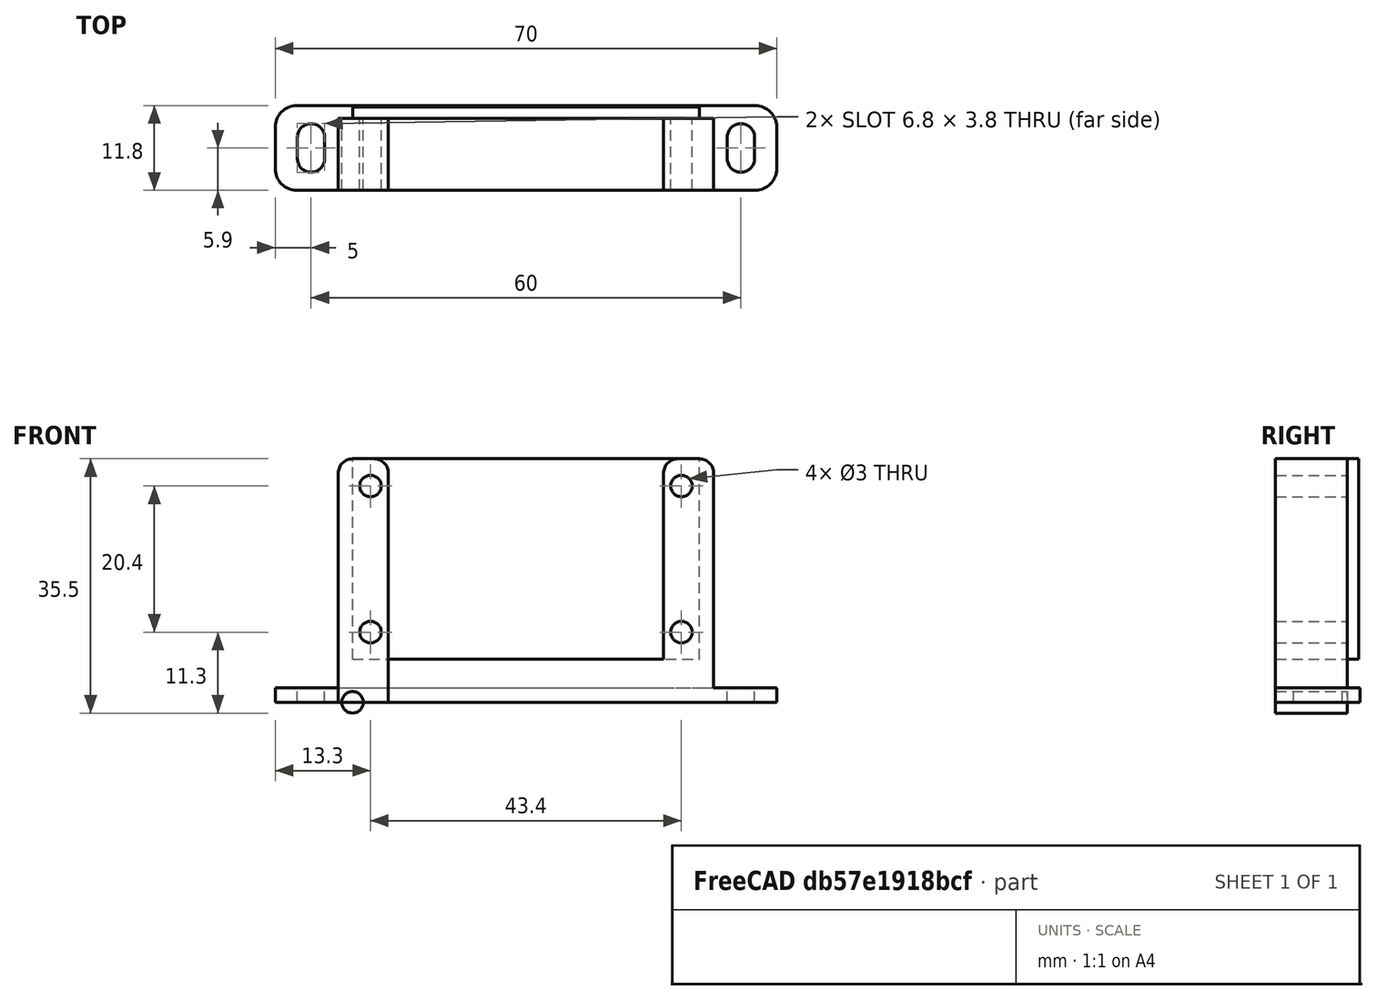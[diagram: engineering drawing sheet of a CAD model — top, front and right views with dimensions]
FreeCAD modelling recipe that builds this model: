
FCSTD DOCUMENT  (FreeCAD 0.19R)
Label: esp8266_wemos
License: All rights reserved
LicenseURL: http://en.wikipedia.org/wiki/All_rights_reserved
objects: Part::Box×3, Part::FeaturePython×2, Part::Cut×2, Spreadsheet::Sheet×1, Part::Cylinder×1, Part::Fillet×1, Part::Feature×1, Part::MultiFuse×1, PartDesign::FeatureBase×1, PartDesign::Body×1
note: 11 computed .brp shape members not serialized (recipe doc carries the construction recipe); baked Part::Feature solids carry a one-line shape summary decoded from their .brp

FEATURE [Part::Box] Box  label="v attachment"
  AttacherType = Attacher::AttachEngine3D
  Height = 34
  Length = 7
  Placement = pos=(-2,0,0) rot=(0,0,1;0rad)
  Width = 10
  expr: .Placement.Base.x = -(<<p>>.hole_stand_length - (<<p>>.pcb_length - <<p>>.hole_dist_length))
  expr: Length = <<p>>.hole_stand_length
  expr: Width = <<p>>.thickness
  expr: Height = <<p>>.pcb_width + <<p>>.bottom_offset
FEATURE [Spreadsheet::Sheet] Spreadsheet  label="p"
  cells = A1=pcb_length; B1(pcb_length)=48.4; A2=pcb_width; B2(pcb_width)=28; A3=pcb_height; B3(pcb_height)=1.6; A4=hole_dist_length; B4(hole_dist_length)=43.4; A5=hole_dist_width; B5(hole_dist_width)=20.4; A6=hole_r; B6(hole_r)=1.5; A7=thickness; B7(thickness)=10; A8=bottom_offset; B8(bottom_offset)=6; A9=hole_stand_length; B9(hole_stand_length)=7
FEATURE [Part::Box] Box001  label="bottom block"
  AttacherType = Attacher::AttachEngine3D
  Height = 6
  Length = 48.4
  Width = 10
  expr: Height = <<p>>.bottom_offset
  expr: Width = <<p>>.thickness
  expr: Length = <<p>>.pcb_length
FEATURE [Part::Box] Box002  label="pcb mockup body"
  AttacherType = Attacher::AttachEngine3D
  Height = 28
  Length = 48.4
  Placement = pos=(0,10,6) rot=(0,0,1;0rad)
  Width = 1.6
  expr: Length = <<p>>.pcb_length
  expr: Width = <<p>>.pcb_height
  expr: Height = <<p>>.pcb_width
  expr: .Placement.Base.z = <<p>>.bottom_offset
  expr: .Placement.Base.y = <<p>>.thickness
FEATURE [Part::Cylinder] Cylinder  label="hole"
  Angle = 360
  AttacherType = Attacher::AttachEngine3D
  Height = 10
  Placement = pos=(0,0,0) rot=(-1,0,0;1.5708rad)
  Radius = 1.5
  expr: Radius = <<p>>.hole_r
FEATURE [Part::FeaturePython] Array001  label="hole array"  # Draft array (typed FeaturePython)
  Angle = 360
  ArrayType = 0
  Axis = (0,0,1)
  Base = -> Cylinder
  Center = (0,0,0)
  Count = 4
  ExpandArray = false
  Fuse = false
  IntervalAxis = (0,0,0)
  IntervalX = (43.4,0,0)
  IntervalY = (0,100,0)
  IntervalZ = (0,0,20.4)
  NumberCircles = 3
  NumberPolar = 5
  NumberX = 2
  NumberY = 1
  NumberZ = 2
  Placement = pos=(2.5,0,9.8) rot=(0,0,1;0rad)
  PlacementList = 4 placements: [(0,0,0),(0,0,20.4),(43.4,0,0),(43.4,0,20.4)]
  RadialDistance = 50
  ScaleList = (4) [(1,1,1),(1,1,1),(1,1,1),(1,1,1)]
  Symmetry = 1
  TangentialDistance = 25
  expr: .IntervalX.x = <<p>>.hole_dist_length
  expr: .IntervalZ.z = <<p>>.hole_dist_width
  expr: .Placement.Base.z = <<p>>.bottom_offset + (<<p>>.pcb_width - <<p>>.hole_dist_width) / 2
  expr: .Placement.Base.x = (<<p>>.pcb_length - <<p>>.hole_dist_length) / 2
FEATURE [Part::Fillet] Fillet  label="v attachment fillet"
  Base = -> Box
  Edges = 2 edges r=2: [Edge2,Edge6]
FEATURE [Part::FeaturePython] Array  label="v attachment array"  # Draft array (typed FeaturePython)
  Angle = 360
  ArrayType = 0
  Axis = (0,0,1)
  Base = -> Fillet
  Center = (0,0,0)
  Count = 2
  ExpandArray = false
  Fuse = false
  IntervalAxis = (0,0,0)
  IntervalX = (45.4,0,0)
  IntervalY = (0,1,0)
  IntervalZ = (0,0,100)
  NumberCircles = 3
  NumberPolar = 5
  NumberX = 2
  NumberY = 1
  NumberZ = 1
  PlacementList = 2 placements: [(0,0,0),(45.4,0,0)]
  RadialDistance = 50
  ScaleList = (2) [(1,1,1),(1,1,1)]
  Symmetry = 1
  TangentialDistance = 25
  expr: .IntervalX.x = <<p>>.hole_dist_length + <<p>>.hole_stand_length - (<<p>>.pcb_length - <<p>>.hole_dist_length)
FEATURE [Part::Cut] Cut001  label="attachment cut"
  Base = -> Array
  Tool = -> Array001
FEATURE [Part::Feature] Cut003001  label="attach plane x dir001"
  Placement = pos=(-10.8,0,0) rot=(0,0,1;0rad)
  shape: bbox 70 x 11.8 x 2 mm, 18 faces (baked)
FEATURE [Part::MultiFuse] Fusion  label="pcb attachment fusion"
  Shapes = -> [Box001,Cut001,Cut003001]
FEATURE [PartDesign::FeatureBase] Clone001
  BaseFeature = -> Array001
  Placement = pos=(2.5,0,9.8) rot=(0,0,1;0rad)
FEATURE [PartDesign::Body] Body001  label="hole array clone"
  BaseFeature = -> Array001
  Group = -> [Clone001]
  Origin = -> Origin001
  Tip = -> Clone001
FEATURE [Part::Cut] Cut  label="pcb mockup"
  Base = -> Box002
  Tool = -> Body001
